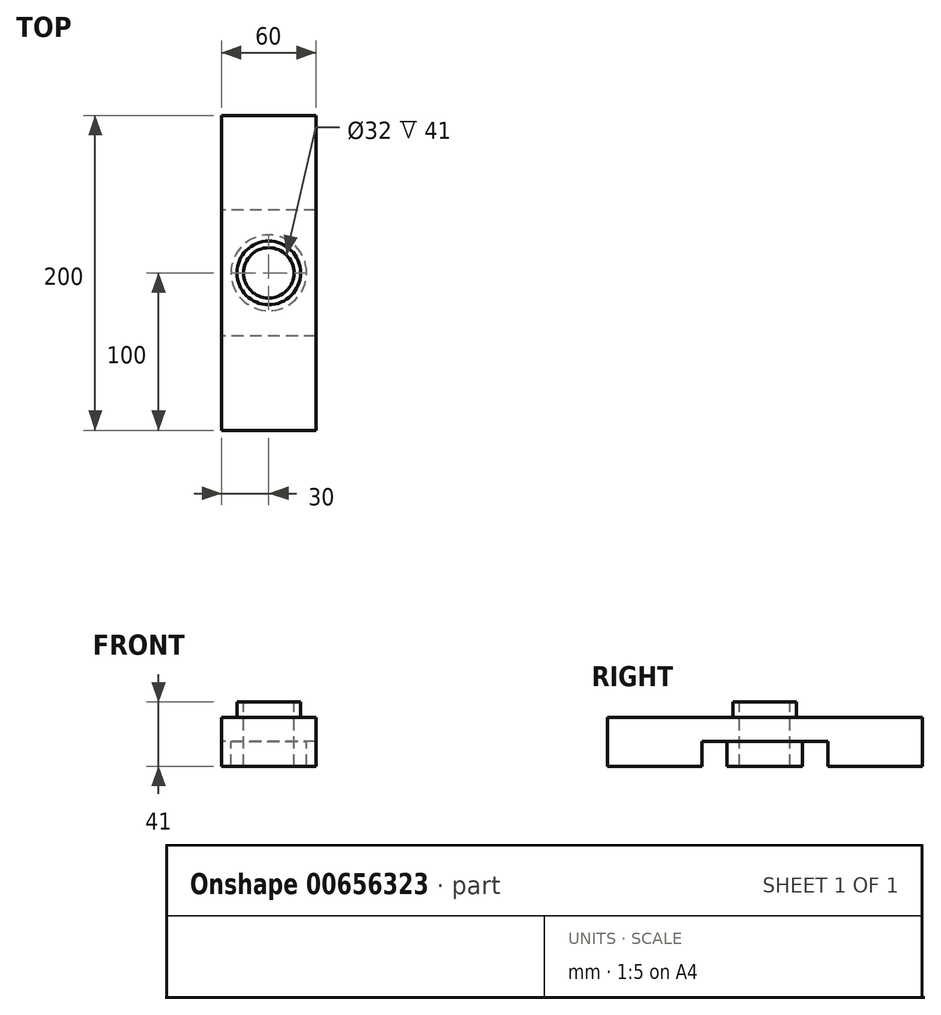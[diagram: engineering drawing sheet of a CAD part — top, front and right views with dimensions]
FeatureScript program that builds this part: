
annotation { "Feature Type Name" : "Feature", "Feature Type Description" : "" }
export const myFeature = defineFeature(function(context is Context, id is Id, definition is map)
    precondition{}
    {
        {
            var Q0;
            Q0=qCreatedBy(makeId("Right.planeOp"),FACE);
            var sketch = newSketch(context, id + "F0", { "sketchPlane" : qUnion([Q0])});
            skLineSegment(sketch, "E0.bottom", {"start": v(-100, 0) * mm, "end": v(100, 0) * mm});
            skLineSegment(sketch, "E0.top", {"start": v(-100, 31) * mm, "end": v(100, 31) * mm});
            skLineSegment(sketch, "E0.left", {"start": v(-100, 0) * mm, "end": v(-100, 31) * mm});
            skLineSegment(sketch, "E0.right", {"start": v(100, 0) * mm, "end": v(100, 31) * mm});
            skLineSegment(sketch, "E1.bottom", {"start": v(0, 0) * mm, "end": v(40, 0) * mm});
            skLineSegment(sketch, "E1.top", {"start": v(0, 16) * mm, "end": v(40, 16) * mm});
            skLineSegment(sketch, "E1.left", {"start": v(0, 0) * mm, "end": v(0, 16) * mm});
            skLineSegment(sketch, "E1.right", {"start": v(40, 0) * mm, "end": v(40, 16) * mm});
            skLineSegment(sketch, "E2.MirrorCS", {"start": v(-40, 0) * mm, "end": v(-40, 16) * mm});
            skLineSegment(sketch, "E3.MirrorCS", {"start": v(0, 16) * mm, "end": v(-40, 16) * mm});
            skLineSegment(sketch, "E4.MirrorCS", {"start": v(0, 0) * mm, "end": v(-40, 0) * mm});
            skSolve(sketch);
        }
        {
            var Q0;
            Q0=makeQuery(id+"F0.imprint","IMPRINT",FACE,{"disambiguationData":[TD([[makeQuery(id+"F0.imprint","IMPRINT",EDGE,{"derivedFrom":sQuery(id+"F0.wireOp",EDGE,"E0.top")}),-1.0]])]});
            extrude(context, id + "F1", {"entities" : qUnion([Q0]), "depth" : 60 * mm, "offsetDistance" : 25 * mm});
        }
        {
            var Q0;
            Q0=makeQuery(id+"F1.opExtrude","SWEPT_FACE",FACE,{"disambiguationData":[OSD([sQuery(id+"F0.wireOp",EDGE,"E0.top")])]});
            var sketch = newSketch(context, id + "F2", { "sketchPlane" : qUnion([Q0])});
            skCircle(sketch, "E5", {"center": v(30, 0) * mm, "radius": 16 * mm});
            skSolve(sketch);
        }
        {
            var Q0;
            Q0=makeQuery(id+"F2.imprint","IMPRINT",FACE,{"disambiguationData":[TD([[makeQuery(id+"F2.imprint","IMPRINT",EDGE,{"derivedFrom":sQuery(id+"F2.wireOp",EDGE,"E5")}),1.0]])]});
            extrude(context, id + "F3", {"entities" : qUnion([Q0]), "operationType" : NewBodyOperationType.REMOVE, "oppositeDirection" : true, "depth" : 25 * mm, "offsetDistance" : 25 * mm});
        }
        {
            var Q0;
            Q0=makeQuery(id+"F1.opExtrude","SWEPT_FACE",FACE,{"disambiguationData":[OSD([sQuery(id+"F0.wireOp",EDGE,"E0.top")])]});
            var sketch = newSketch(context, id + "F4", { "sketchPlane" : qUnion([Q0])});
            skCircle(sketch, "E6", {"center": v(30, 0) * mm, "radius": 20.23 * mm});
            skCircle(sketch, "E7", {"center": v(30, 0) * mm, "radius": 16 * mm});
            skSolve(sketch);
        }
        {
            var Q0;
            Q0=makeQuery(id+"F4.imprint","IMPRINT",FACE,{"disambiguationData":[TD([[makeQuery(id+"F4.imprint","IMPRINT",EDGE,{"derivedFrom":sQuery(id+"F4.wireOp",EDGE,"E6")}),1.0]])]});
            extrude(context, id + "F5", {"entities" : qUnion([Q0]), "operationType" : NewBodyOperationType.ADD, "depth" : 10 * mm, "offsetDistance" : 25 * mm});
        }
        {
            var Q0;
            Q0=makeQuery(id+"F1.opExtrude","SWEPT_FACE",FACE,{"disambiguationData":[OSD([sQuery(id+"F0.wireOp",EDGE,"E1.top"),sQuery(id+"F0.wireOp",EDGE,"E3.MirrorCS")])]});
            var sketch = newSketch(context, id + "F6", { "sketchPlane" : qUnion([Q0])});
            skCircle(sketch, "E8", {"center": v(30, 0) * mm, "radius": 24 * mm});
            skCircle(sketch, "E9", {"center": v(30, 0) * mm, "radius": 16 * mm});
            skSolve(sketch);
        }
        {
            var Q0;
            Q0=makeQuery(id+"F6.imprint","IMPRINT",FACE,{"disambiguationData":[TD([[makeQuery(id+"F6.imprint","IMPRINT",EDGE,{"derivedFrom":sQuery(id+"F6.wireOp",EDGE,"E8")}),1.0]])]});
            extrude(context, id + "F7", {"entities" : qUnion([Q0]), "operationType" : NewBodyOperationType.ADD, "depth" : 16 * mm, "offsetDistance" : 25 * mm});
        }
    });
